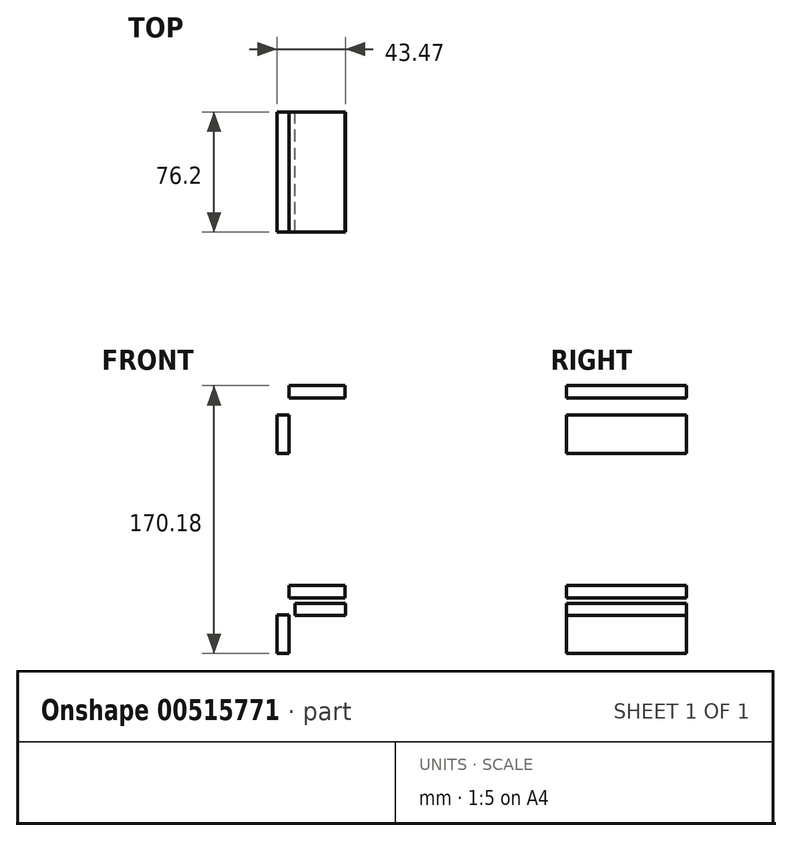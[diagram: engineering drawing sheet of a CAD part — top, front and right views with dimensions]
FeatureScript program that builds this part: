
annotation { "Feature Type Name" : "Feature", "Feature Type Description" : "" }
export const myFeature = defineFeature(function(context is Context, id is Id, definition is map)
    precondition{}
    {
        {
            var Q0;
            Q0=qCreatedBy(makeId("Front.planeOp"),FACE);
            var sketch = newSketch(context, id + "F0", { "sketchPlane" : qUnion([Q0])});
            skLineSegment(sketch, "E0.bottom", {"start": v(0, 0) * mm, "end": v(-7.62, 0) * mm});
            skLineSegment(sketch, "E0.top", {"start": v(0, 43.18) * mm, "end": v(-7.62, 43.18) * mm});
            skLineSegment(sketch, "E0.left", {"start": v(0, 0) * mm, "end": v(0, 43.18) * mm});
            skLineSegment(sketch, "E0.right", {"start": v(-7.62, 0) * mm, "end": v(-7.62, 43.18) * mm});
            skLineSegment(sketch, "E1.bottom", {"start": v(3.68, 0) * mm, "end": v(11.3, 0) * mm});
            skLineSegment(sketch, "E1.top", {"start": v(3.68, 31.75) * mm, "end": v(11.3, 31.75) * mm});
            skLineSegment(sketch, "E1.left", {"start": v(3.68, 0) * mm, "end": v(3.68, 31.75) * mm});
            skLineSegment(sketch, "E1.right", {"start": v(11.3, 0) * mm, "end": v(11.3, 31.75) * mm});
            skLineSegment(sketch, "E2.bottom", {"start": v(0, 43.18) * mm, "end": v(35.56, 43.18) * mm});
            skLineSegment(sketch, "E2.top", {"start": v(0, 35.43) * mm, "end": v(35.56, 35.43) * mm});
            skLineSegment(sketch, "E2.left", {"start": v(0, 43.18) * mm, "end": v(0, 35.43) * mm});
            skLineSegment(sketch, "E2.right", {"start": v(35.56, 43.18) * mm, "end": v(35.56, 35.43) * mm});
            skLineSegment(sketch, "E3.bottom", {"start": v(11.3, 31.75) * mm, "end": v(35.85, 31.75) * mm});
            skLineSegment(sketch, "E3.top", {"start": v(11.3, 24.28) * mm, "end": v(35.85, 24.28) * mm});
            skLineSegment(sketch, "E3.left", {"start": v(11.3, 31.75) * mm, "end": v(11.3, 24.28) * mm});
            skLineSegment(sketch, "E3.right", {"start": v(35.85, 31.75) * mm, "end": v(35.85, 24.28) * mm});
            skLineSegment(sketch, "E4.bottom", {"start": v(35.56, 43.18) * mm, "end": v(-7.62, 43.18) * mm});
            skLineSegment(sketch, "E4.top", {"start": v(35.56, 24.43) * mm, "end": v(-7.62, 24.43) * mm});
            skLineSegment(sketch, "E4.left", {"start": v(35.56, 43.18) * mm, "end": v(35.56, 24.43) * mm});
            skLineSegment(sketch, "E4.right", {"start": v(-7.62, 43.18) * mm, "end": v(-7.62, 24.43) * mm});
            skLineSegment(sketch, "E5.bottom", {"start": v(11.3, 24.28) * mm, "end": v(-7.62, 24.28) * mm});
            skLineSegment(sketch, "E5.top", {"start": v(11.3, 0) * mm, "end": v(-7.62, 0) * mm});
            skLineSegment(sketch, "E5.left", {"start": v(11.3, 24.28) * mm, "end": v(11.3, 0) * mm});
            skLineSegment(sketch, "E5.right", {"start": v(-7.62, 24.28) * mm, "end": v(-7.62, 0) * mm});
            skSolve(sketch);
        }
        {
            var Q0;
            {var subQ5=sQuery(id+"F0.wireOp",EDGE,"E5.right");Q0=makeQuery(id+"F0.imprint","IMPRINT",FACE,{"disambiguationData":[TD([[makeQuery(id+"F0.imprint","IMPRINT",EDGE,{"derivedFrom":subQ5}),1.0]])]});}
            var Q1;
            {var subQ5=sQuery(id+"F0.wireOp",EDGE,"E5.left");Q1=makeQuery(id+"F0.imprint","IMPRINT",FACE,{"disambiguationData":[TD([[makeQuery(id+"F0.imprint","IMPRINT",EDGE,{"derivedFrom":subQ5}),-1.0]])]});}
            var Q2;
            {var subQ0=sQuery(id+"F0.wireOp",EDGE,"E2.top");Q2=makeQuery(id+"F0.imprint","IMPRINT",FACE,{"disambiguationData":[TD([[makeQuery(id+"F0.imprint","IMPRINT",EDGE,{"derivedFrom":subQ0}),1.0]])]});}
            var Q3;
            {var subQ2=sQuery(id+"F0.wireOp",EDGE,"E3.top");Q3=makeQuery(id+"F0.imprint","IMPRINT",FACE,{"disambiguationData":[TD([[makeQuery(id+"F0.imprint","IMPRINT",EDGE,{"derivedFrom":subQ2}),1.0]])]});}
            var Q4;
            {var subQ5=sQuery(id+"F0.wireOp",EDGE,"E0.right");Q4=makeQuery(id+"F0.imprint","IMPRINT",FACE,{"disambiguationData":[TD([[makeQuery(id+"F0.imprint","IMPRINT",EDGE,{"derivedFrom":subQ5}),-1.0]])]});}
            var Q5;
            {var subQ4=sQuery(id+"F0.wireOp",EDGE,"E2.left");Q5=makeQuery(id+"F0.imprint","IMPRINT",FACE,{"disambiguationData":[TD([[makeQuery(id+"F0.imprint","IMPRINT",EDGE,{"derivedFrom":subQ4}),-1.0]])]});}
            var Q6;
            {var subQ3=sQuery(id+"F0.wireOp",EDGE,"E4.left");var subQ5=sQuery(id+"F0.wireOp",EDGE,"E4.top");var subQ7=makeQuery(id+"F0.imprint","INTERSECT",VERTEX,{"derivedFrom":[subQ5,subQ3]});Q6=makeQuery(id+"F0.imprint","IMPRINT",FACE,{"disambiguationData":[TD([[makeQuery(id+"F0.imprint","IMPRINT",EDGE,{"disambiguationData":[TD([[subQ7,-1.0]])],"derivedFrom":subQ5}),-1.0]])]});}
            var Q7;
            {var subQ0=sQuery(id+"F0.wireOp",EDGE,"E5.bottom");var subQ1=sQuery(id+"F0.wireOp",EDGE,"E1.left");var subQ2=makeQuery(id+"F0.imprint","INTERSECT",VERTEX,{"derivedFrom":[subQ1,subQ0]});Q7=makeQuery(id+"F0.imprint","IMPRINT",FACE,{"disambiguationData":[TD([[makeQuery(id+"F0.imprint","IMPRINT",EDGE,{"disambiguationData":[TD([[subQ2,-1.0]])],"derivedFrom":subQ1}),-1.0]])]});}
            var Q8;
            {var subQ0=sQuery(id+"F0.wireOp",EDGE,"E1.top");Q8=makeQuery(id+"F0.imprint","IMPRINT",FACE,{"disambiguationData":[TD([[makeQuery(id+"F0.imprint","IMPRINT",EDGE,{"derivedFrom":subQ0}),-1.0]])]});}
            extrude(context, id + "F1", {"entities" : qUnion([Q0, Q1, Q2, Q3, Q4, Q5, Q6, Q7, Q8]), "depth" : 76.2 * mm, "offsetDistance" : 25.4 * mm});
        }
        {
            var Q0;
            Q0=makeQuery(id+"F1.opExtrude","SWEPT_BODY",BODY,{"disambiguationData":[OSD([sQuery(id+"F0.wireOp",EDGE,"E0.left"),sQuery(id+"F0.wireOp",EDGE,"E0.right"),sQuery(id+"F0.wireOp",EDGE,"E2.top"),sQuery(id+"F0.wireOp",EDGE,"E4.bottom"),sQuery(id+"F0.wireOp",EDGE,"E4.left"),sQuery(id+"F0.wireOp",EDGE,"E4.right"),sQuery(id+"F0.wireOp",EDGE,"E5.top"),sQuery(id+"F0.wireOp",EDGE,"E5.right")])]});
            var Q1;
            Q1=qCreatedBy(makeId("Top.planeOp"),FACE);
            transform(context, id + "F2", {"entities" : qUnion([Q0]), "transformType" : TransformType.TRANSLATION_DISTANCE, "transformDirection" : qUnion([Q1]), "distance" : 127 * mm, "makeCopy" : true});
        }
    });
